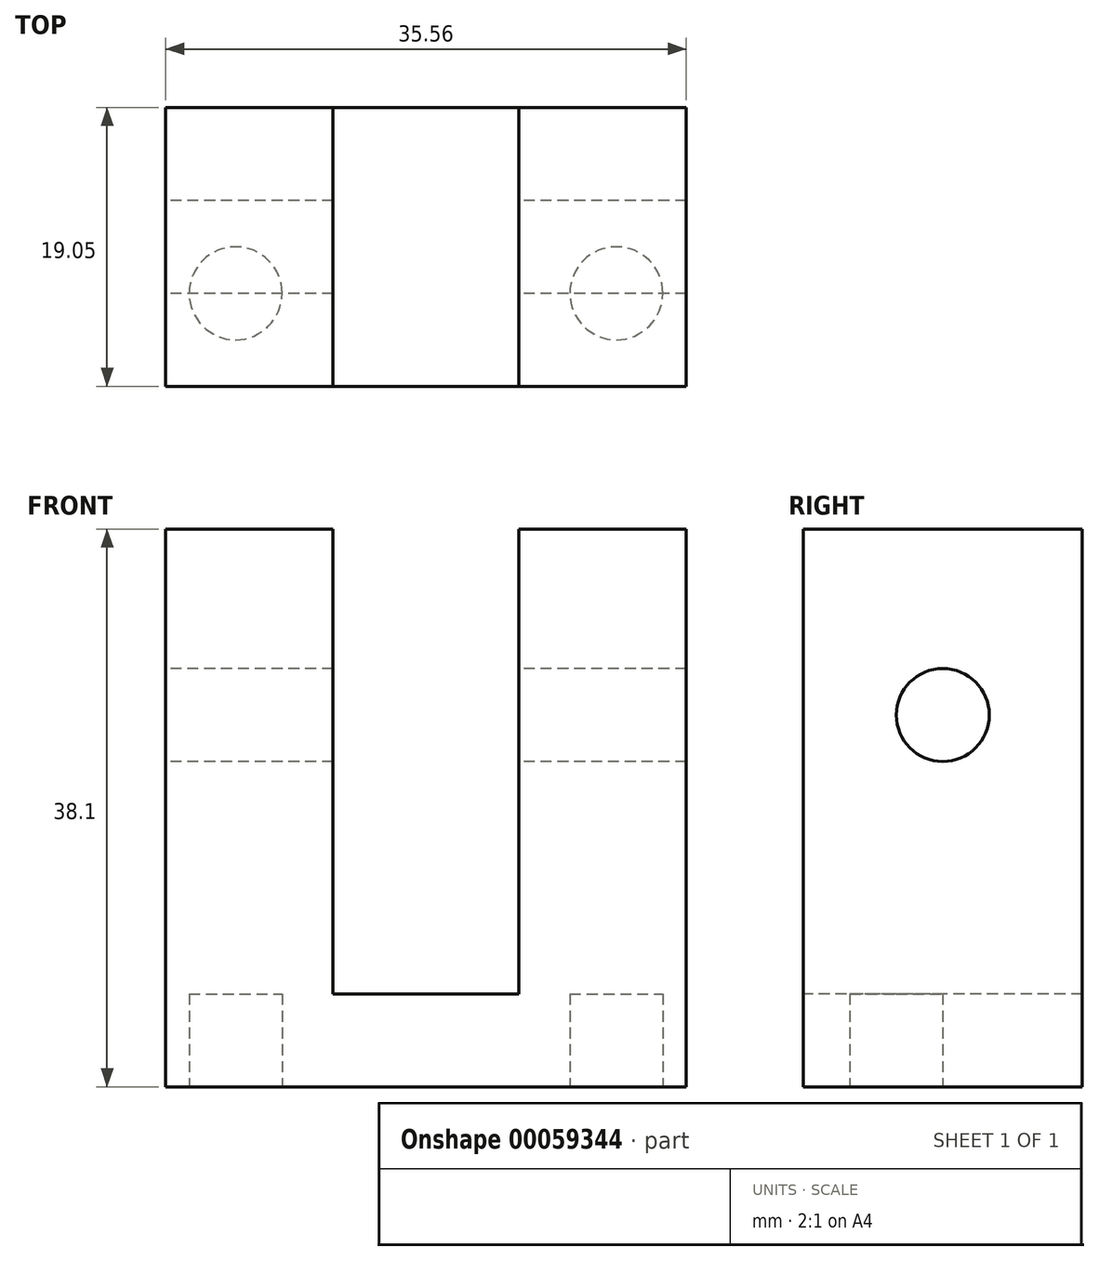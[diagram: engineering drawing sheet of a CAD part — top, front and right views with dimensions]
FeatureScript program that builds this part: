
annotation { "Feature Type Name" : "Feature", "Feature Type Description" : "" }
export const myFeature = defineFeature(function(context is Context, id is Id, definition is map)
    precondition{}
    {
        {
            var Q0;
            Q0=qCreatedBy(makeId("Right.planeOp"),FACE);
            var sketch = newSketch(context, id + "F0", { "sketchPlane" : qUnion([Q0])});
            skLineSegment(sketch, "E0.bottom", {"start": v(-9.4, 18.63) * mm, "end": v(9.66, 18.63) * mm});
            skLineSegment(sketch, "E0.top", {"start": v(-9.4, -19.47) * mm, "end": v(9.66, -19.47) * mm});
            skLineSegment(sketch, "E0.left", {"start": v(-9.4, 18.63) * mm, "end": v(-9.4, -19.47) * mm});
            skLineSegment(sketch, "E0.right", {"start": v(9.66, 18.63) * mm, "end": v(9.66, -19.47) * mm});
            skCircle(sketch, "E1", {"center": v(0.13, 5.93) * mm, "radius": 3.18 * mm});
            skSolve(sketch);
        }
        {
            var Q0;
            Q0 = qSketchRegion(id + "F0", true);
            extrude(context, id + "F1", {"entities" : qUnion([Q0]), "depth" : 35.56 * mm});
        }
        {
            var Q0;
            Q0=makeQuery(id+"F1.opExtrude","SWEPT_FACE",FACE,{"disambiguationData":[OSD([sQuery(id+"F0.wireOp",EDGE,"E0.top")])]});
            var sketch = newSketch(context, id + "F2", { "sketchPlane" : qUnion([Q0])});
            skCircle(sketch, "E2", {"center": v(4.78, 3.04) * mm, "radius": 3.18 * mm});
            skCircle(sketch, "E3", {"center": v(30.78, 3.04) * mm, "radius": 3.18 * mm});
            skSolve(sketch);
        }
        {
            var Q0;
            Q0 = qSketchRegion(id + "F2", true);
            extrude(context, id + "F3", {"entities" : qUnion([Q0]), "operationType" : NewBodyOperationType.REMOVE, "oppositeDirection" : true, "depth" : 6.35 * mm});
        }
        {
            var Q0;
            Q0=makeQuery(id+"F1.opExtrude","SWEPT_FACE",FACE,{"disambiguationData":[OSD([sQuery(id+"F0.wireOp",EDGE,"E0.left")])]});
            var sketch = newSketch(context, id + "F4", { "sketchPlane" : qUnion([Q0])});
            skLineSegment(sketch, "E4.bottom", {"start": v(11.43, 18.63) * mm, "end": v(24.13, 18.63) * mm});
            skLineSegment(sketch, "E4.top", {"start": v(11.43, -13.12) * mm, "end": v(24.13, -13.12) * mm});
            skLineSegment(sketch, "E4.left", {"start": v(11.43, 18.63) * mm, "end": v(11.43, -13.12) * mm});
            skLineSegment(sketch, "E4.right", {"start": v(24.13, 18.63) * mm, "end": v(24.13, -13.12) * mm});
            skSolve(sketch);
        }
        {
            var Q0;
            Q0 = qSketchRegion(id + "F4", true);
            extrude(context, id + "F5", {"entities" : qUnion([Q0]), "operationType" : NewBodyOperationType.REMOVE, "oppositeDirection" : true, "depth" : 35.56 * mm});
        }
    });
